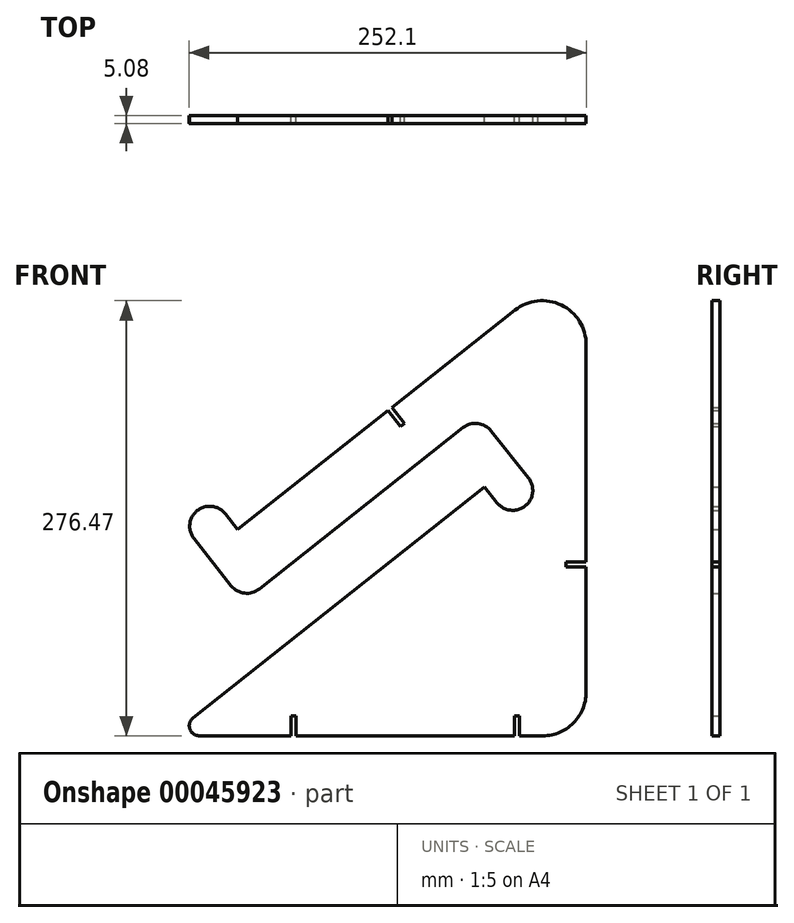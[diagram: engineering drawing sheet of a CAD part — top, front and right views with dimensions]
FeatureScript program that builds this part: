
annotation { "Feature Type Name" : "Feature", "Feature Type Description" : "" }
export const myFeature = defineFeature(function(context is Context, id is Id, definition is map)
    precondition{}
    {
        {
            var Q0;
            Q0=qCreatedBy(makeId("Front.planeOp"),FACE);
            var sketch = newSketch(context, id + "F0", { "sketchPlane" : qUnion([Q0])});
            skLineSegment(sketch, "E0", {"start": v(-104.64, 141.14) * mm, "end": v(-104.64, 141.14) * mm});
            skLineSegment(sketch, "E1", {"start": v(-86.8, 139.06) * mm, "end": v(-78.91, 129.1) * mm});
            skLineSegment(sketch, "E2", {"start": v(-106.71, 123.3) * mm, "end": v(-83.07, 93.43) * mm});
            skLineSegment(sketch, "E3", {"start": v(-65.22, 91.35) * mm, "end": v(64.23, 193.82) * mm});
            skLineSegment(sketch, "E4", {"start": v(82.07, 191.74) * mm, "end": v(105.71, 161.87) * mm});
            skLineSegment(sketch, "E5", {"start": v(103.64, 144.03) * mm, "end": v(103.64, 144.03) * mm});
            skLineSegment(sketch, "E6", {"start": v(85.8, 146.1) * mm, "end": v(77.92, 156.06) * mm});
            skLineSegment(sketch, "E7", {"start": v(77.92, 156.06) * mm, "end": v(-107.3, 9.45) * mm});
            skPoint(sketch, "E8.visualSharp", {"position": v(93.68, 136.15) * mm});
            skArc(sketch, "E8.filletArc", {"start": v(85.8, 146.1) * mm, "mid": v(94.29, 141.37) * mm, "end": v(103.64, 144.03) * mm});
            skPoint(sketch, "E9.visualSharp", {"position": v(113.6, 151.91) * mm});
            skArc(sketch, "E9.filletArc", {"start": v(103.64, 144.03) * mm, "mid": v(108.37, 152.52) * mm, "end": v(105.71, 161.87) * mm});
            skPoint(sketch, "E10.visualSharp", {"position": v(-94.68, 149.02) * mm});
            skArc(sketch, "E10.filletArc", {"start": v(-86.8, 139.06) * mm, "mid": v(-95.29, 143.8) * mm, "end": v(-104.64, 141.14) * mm});
            skPoint(sketch, "E11.visualSharp", {"position": v(-114.6, 133.26) * mm});
            skArc(sketch, "E11.filletArc", {"start": v(-104.64, 141.14) * mm, "mid": v(-109.37, 132.65) * mm, "end": v(-106.71, 123.3) * mm});
            skPoint(sketch, "E12.visualSharp", {"position": v(-75.18, 83.47) * mm});
            skArc(sketch, "E12.filletArc", {"start": v(-83.07, 93.43) * mm, "mid": v(-74.57, 88.7) * mm, "end": v(-65.22, 91.35) * mm});
            skPoint(sketch, "E13.visualSharp", {"position": v(74.19, 201.7) * mm});
            skArc(sketch, "E13.filletArc", {"start": v(82.07, 191.74) * mm, "mid": v(73.58, 196.48) * mm, "end": v(64.23, 193.82) * mm});
            skPoint(sketch, "E14.visualSharp", {"position": v(142.39, 0) * mm});
            skPoint(sketch, "E15.visualSharp", {"position": v(142.39, 304.28) * mm});
            skLineSegment(sketch, "E16", {"start": v(142.39, 246.53) * mm, "end": v(142.39, 108.65) * mm});
            skLineSegment(sketch, "E17", {"start": v(97.1, 268.44) * mm, "end": v(18.94, 206.56) * mm});
            skArc(sketch, "E18.filletArc", {"start": v(142.39, 246.53) * mm, "mid": v(126.61, 271.68) * mm, "end": v(97.1, 268.44) * mm});
            skArc(sketch, "E19.filletArc", {"start": v(111.82, -1.88) * mm, "mid": v(133.25, 5.27) * mm, "end": v(142.39, 25.94) * mm});
            skLineSegment(sketch, "E20", {"start": v(16.45, 204.6) * mm, "end": v(24.33, 194.64) * mm});
            skLineSegment(sketch, "E21", {"start": v(24.33, 194.64) * mm, "end": v(26.82, 196.6) * mm});
            skLineSegment(sketch, "E22", {"start": v(26.82, 196.6) * mm, "end": v(18.94, 206.56) * mm});
            skLineSegment(sketch, "E23.trimOffspring", {"start": v(16.45, 204.6) * mm, "end": v(-78.91, 129.1) * mm});
            skLineSegment(sketch, "E24", {"start": v(142.39, 108.65) * mm, "end": v(129.69, 108.65) * mm});
            skLineSegment(sketch, "E25", {"start": v(129.69, 108.65) * mm, "end": v(129.69, 105.47) * mm});
            skLineSegment(sketch, "E26", {"start": v(129.69, 105.47) * mm, "end": v(142.39, 105.47) * mm});
            skLineSegment(sketch, "E27.trimOffspring", {"start": v(142.39, 105.47) * mm, "end": v(142.39, 25.94) * mm});
            skLineSegment(sketch, "E28", {"start": v(111.82, -1.88) * mm, "end": v(99.94, -1.88) * mm});
            skPoint(sketch, "E29.visualSharp", {"position": v(-121.62, -1.88) * mm});
            skArc(sketch, "E29.filletArc", {"start": v(-107.3, 9.45) * mm, "mid": v(-109.36, 2.38) * mm, "end": v(-103.36, -1.88) * mm});
            skLineSegment(sketch, "E30.top", {"start": v(96.76, 10.82) * mm, "end": v(99.94, 10.82) * mm});
            skLineSegment(sketch, "E30.left", {"start": v(96.76, -1.88) * mm, "end": v(96.76, 10.82) * mm});
            skLineSegment(sketch, "E30.right", {"start": v(99.94, -1.88) * mm, "end": v(99.94, 10.82) * mm});
            skLineSegment(sketch, "E31.top", {"start": v(-45.05, 10.82) * mm, "end": v(-41.87, 10.82) * mm});
            skLineSegment(sketch, "E31.left", {"start": v(-45.05, -1.88) * mm, "end": v(-45.05, 10.82) * mm});
            skLineSegment(sketch, "E31.right", {"start": v(-41.87, -1.88) * mm, "end": v(-41.87, 10.82) * mm});
            skLineSegment(sketch, "E32.trimOffspring", {"start": v(-45.05, -1.88) * mm, "end": v(-103.36, -1.88) * mm});
            skLineSegment(sketch, "E33.trimOffspring", {"start": v(96.76, -1.88) * mm, "end": v(-41.87, -1.88) * mm});
            skSolve(sketch);
        }
        {
            var Q0;
            Q0 = qSketchRegion(id + "F0", true);
            extrude(context, id + "F1", {"entities" : qUnion([Q0]), "depth" : 5.08 * mm});
        }
    });
